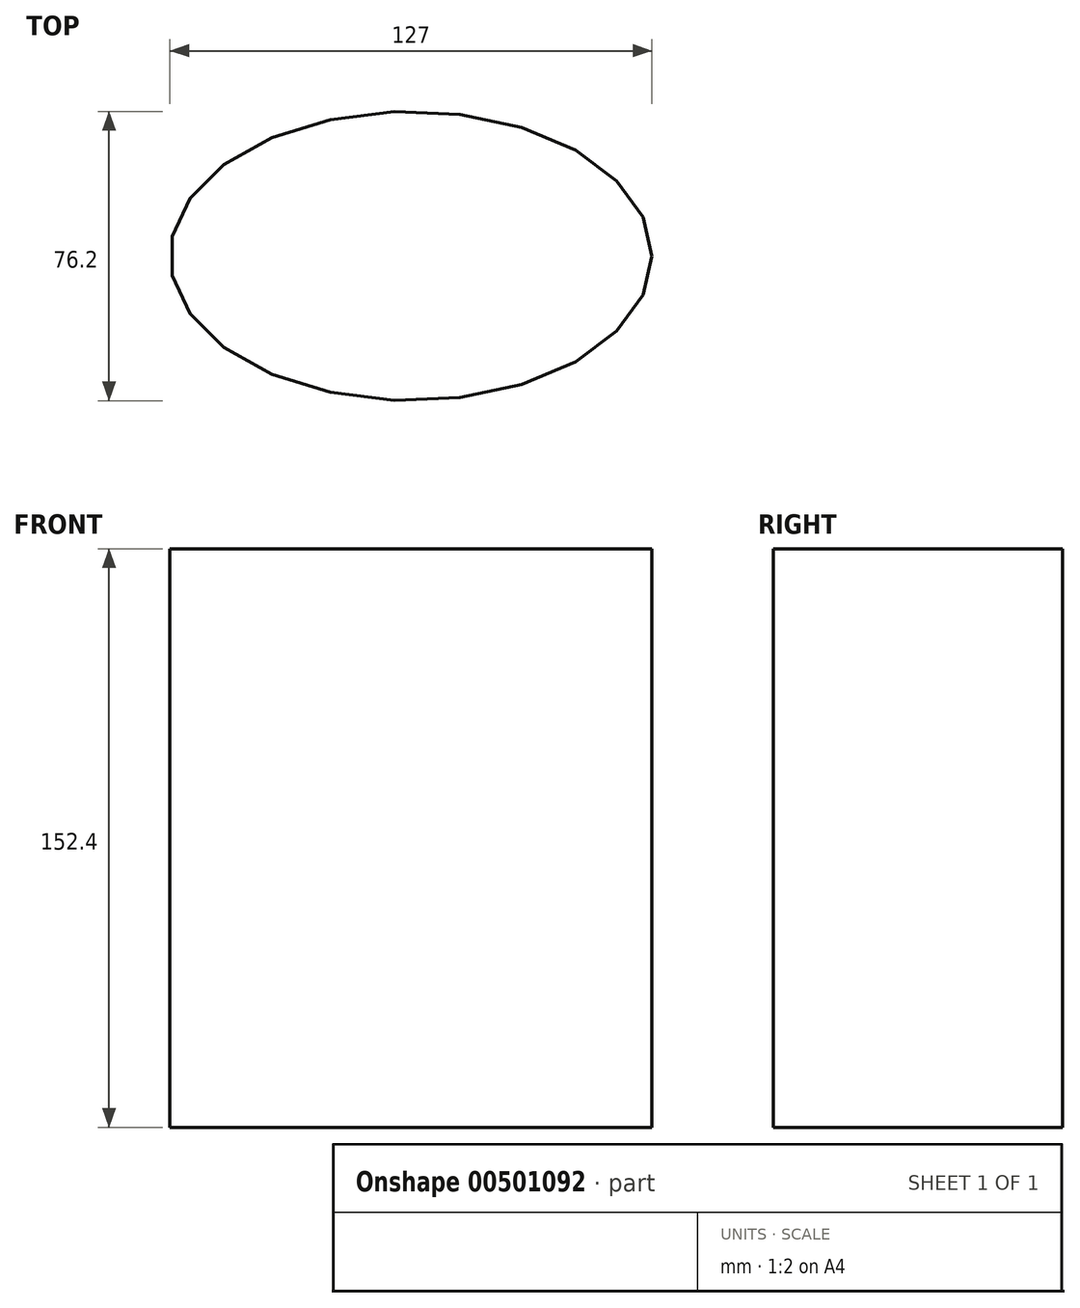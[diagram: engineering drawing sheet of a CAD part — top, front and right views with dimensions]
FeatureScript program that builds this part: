
annotation { "Feature Type Name" : "Feature", "Feature Type Description" : "" }
export const myFeature = defineFeature(function(context is Context, id is Id, definition is map)
    precondition{}
    {
        {
            var Q0;
            Q0=qCreatedBy(makeId("Top.planeOp"),FACE);
            var sketch = newSketch(context, id + "F0", { "sketchPlane" : qUnion([Q0])});
            skEllipse(sketch, "E0", {"center": v(0, 0) * mm, "majorRadius": 63.5 * mm, "minorRadius": 38.1 * mm, "majorAxis": v(1, 0)});
            skSolve(sketch);
        }
        {
            var Q0;
            Q0 = qSketchRegion(id + "F0", true);
            extrude(context, id + "F1", {"entities" : qUnion([Q0]), "depth" : 152.4 * mm});
        }
    });
